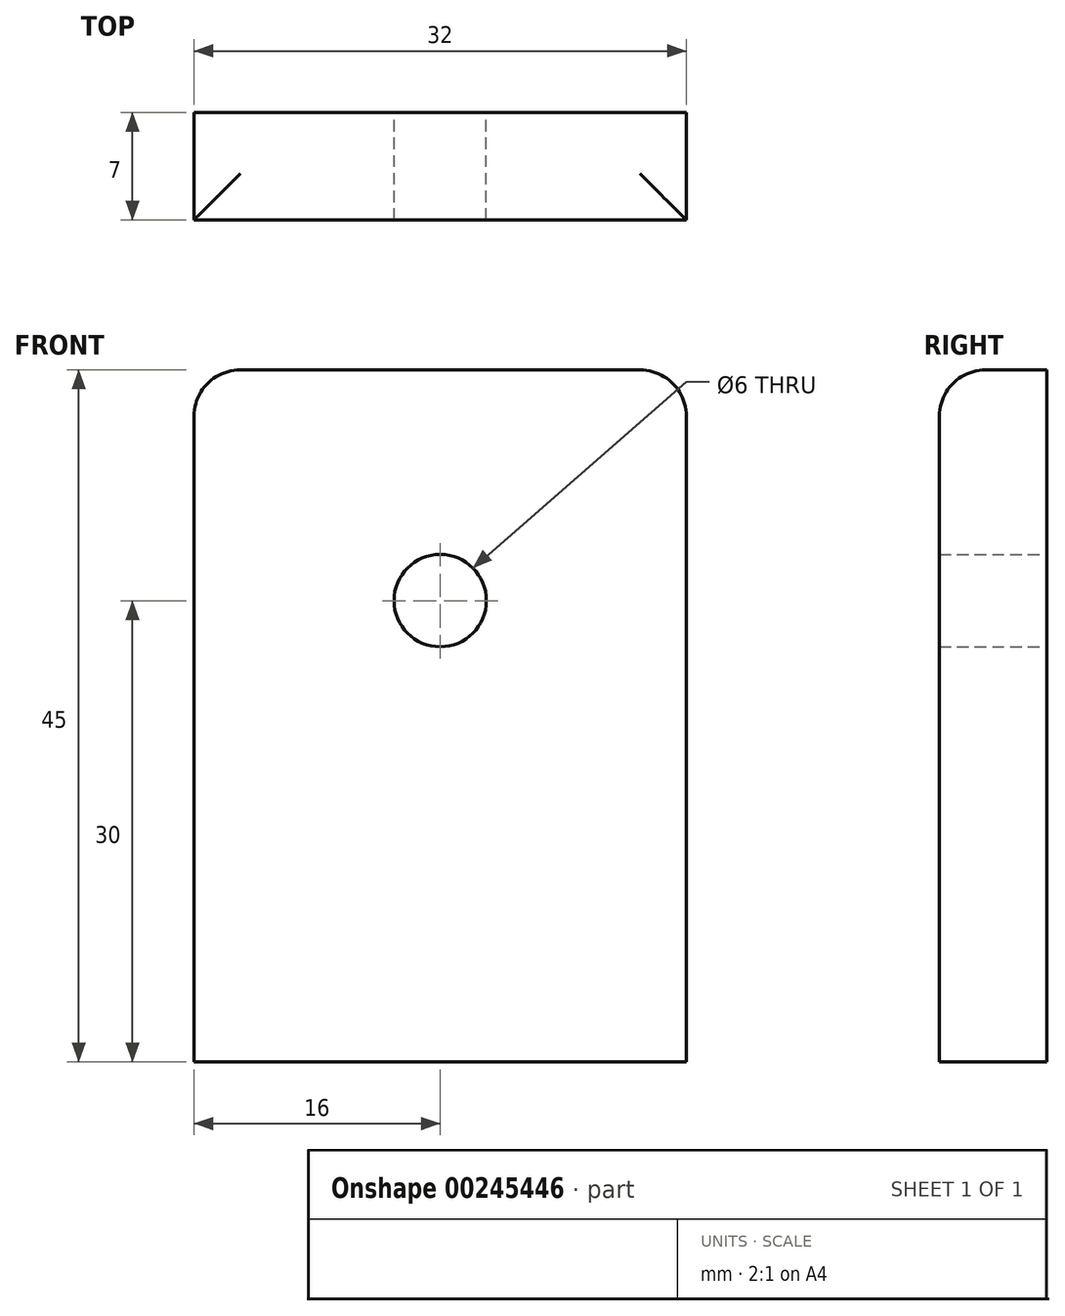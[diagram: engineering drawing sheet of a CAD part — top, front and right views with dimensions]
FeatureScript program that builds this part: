
annotation { "Feature Type Name" : "Feature", "Feature Type Description" : "" }
export const myFeature = defineFeature(function(context is Context, id is Id, definition is map)
    precondition{}
    {
        {
            var Q0;
            Q0=qCreatedBy(makeId("Front.planeOp"),FACE);
            var sketch = newSketch(context, id + "F0", { "sketchPlane" : qUnion([Q0])});
            skLineSegment(sketch, "E0.bottom", {"start": v(0, 0) * mm, "end": v(32, 0) * mm});
            skLineSegment(sketch, "E0.top", {"start": v(0, 45) * mm, "end": v(32, 45) * mm});
            skLineSegment(sketch, "E0.left", {"start": v(0, 0) * mm, "end": v(0, 45) * mm});
            skLineSegment(sketch, "E0.right", {"start": v(32, 0) * mm, "end": v(32, 45) * mm});
            skCircle(sketch, "E1", {"center": v(16, 30) * mm, "radius": 3 * mm});
            skSolve(sketch);
        }
        {
            var Q0;
            Q0 = qSketchRegion(id + "F0", true);
            extrude(context, id + "F1", {"entities" : qUnion([Q0]), "depth" : 7 * mm});
        }
        {
            var Q0;
            Q0=makeQuery(id+"F1.opExtrude","SWEPT_EDGE",EDGE,{"disambiguationData":[OSD([sQuery(id+"F0.wireOp",EDGE,"E0.top"),sQuery(id+"F0.wireOp",EDGE,"E0.right")])]});
            var Q1;
            Q1=makeQuery(id+"F1.opExtrude","SWEPT_EDGE",EDGE,{"disambiguationData":[OSD([sQuery(id+"F0.wireOp",EDGE,"E0.top"),sQuery(id+"F0.wireOp",EDGE,"E0.left")])]});
            var Q2;
            Q2=makeQuery(id+"F1.opExtrude","CAP_EDGE",EDGE,{"disambiguationData":[OSD([sQuery(id+"F0.wireOp",EDGE,"E0.top")])],"isStart":false});
            fillet(context, id + "F2", {"entities" : qUnion([Q0, Q1, Q2]), "radius" : 3 * mm, "tangentPropagation" : true, "allowEdgeOverflow" : false});
        }
    });
